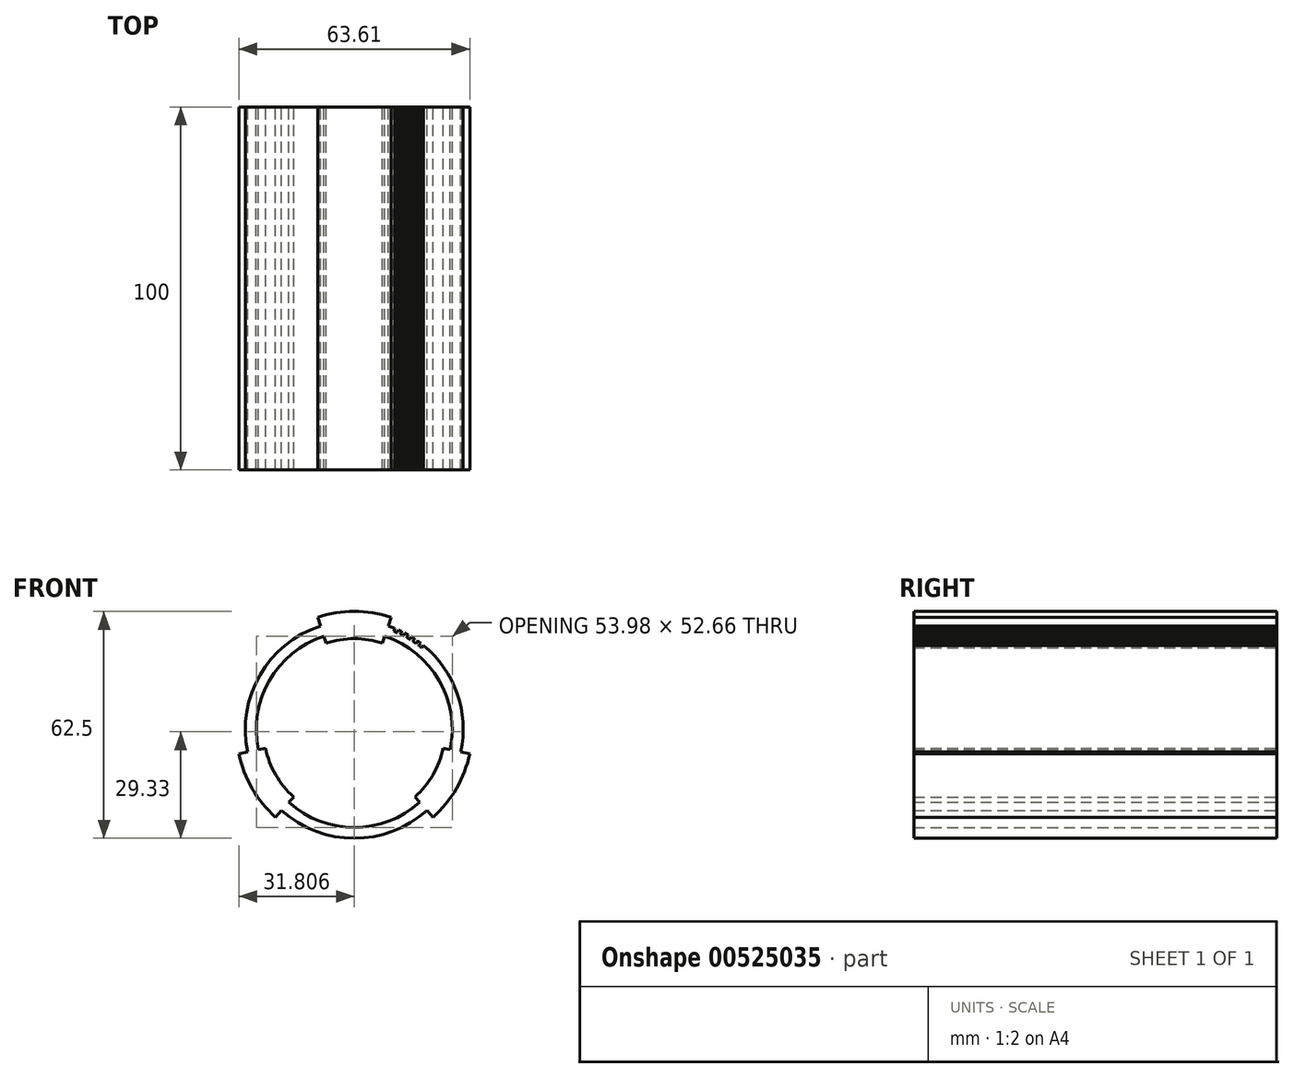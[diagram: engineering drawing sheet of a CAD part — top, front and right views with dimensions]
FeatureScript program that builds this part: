
annotation { "Feature Type Name" : "Feature", "Feature Type Description" : "" }
export const myFeature = defineFeature(function(context is Context, id is Id, definition is map)
    precondition{}
    {
        {
            var Q0;
            Q0=qCreatedBy(makeId("Front.planeOp"),FACE);
            var sketch = newSketch(context, id + "F0", { "sketchPlane" : qUnion([Q0])});
            skArc(sketch, "E0", {"start": v(-14.55, 20.43) * mm, "mid": v(-31.2, 6.92) * mm, "end": v(-34.58, -14.27) * mm});
            skArc(sketch, "E1.0", {"start": v(-13.61, 17.58) * mm, "mid": v(-28.6, 5.42) * mm, "end": v(-31.64, -13.65) * mm});
            skLineSegment(sketch, "E2", {"start": v(-13, 15.68) * mm, "end": v(-13.61, 17.58) * mm});
            skLineSegment(sketch, "E3.MirrorCS", {"start": v(2.54, 15.68) * mm, "end": v(3.17, 17.58) * mm});
            skArc(sketch, "E4.trimOffspring", {"start": v(4.87, 22.8) * mm, "mid": v(-5.22, 24.42) * mm, "end": v(-15.32, 22.8) * mm});
            skArc(sketch, "E5.trimOffspring", {"start": v(2.54, 15.68) * mm, "mid": v(-5.22, 16.92) * mm, "end": v(-13, 15.68) * mm});
            skPoint(sketch, "E6.start.orphan", {"position": v(-15.32, -38.97) * mm});
            skPoint(sketch, "E7.trimOffspring.end.orphan", {"position": v(4.87, -38.97) * mm});
            skLineSegment(sketch, "E8.trimOffspring", {"start": v(-14.55, 20.43) * mm, "end": v(-15.32, 22.8) * mm});
            skLineSegment(sketch, "E9.trimOffspring", {"start": v(4.1, 20.43) * mm, "end": v(4.87, 22.8) * mm});
            skLineSegment(sketch, "E10", {"start": v(-5.22, -8.08) * mm, "end": v(-5.22, 24.42) * mm});
            skArc(sketch, "E11.1.0", {"start": v(-37.03, -14.78) * mm, "mid": v(-33.37, -24.33) * mm, "end": v(-26.93, -32.27) * mm});
            skArc(sketch, "E11.1.1", {"start": v(-29.69, -13.23) * mm, "mid": v(-26.88, -20.58) * mm, "end": v(-21.92, -26.7) * mm});
            skLineSegment(sketch, "E11.1.2", {"start": v(-25.26, -30.41) * mm, "end": v(-26.93, -32.27) * mm});
            skLineSegment(sketch, "E11.1.3", {"start": v(-21.92, -26.7) * mm, "end": v(-23.25, -28.18) * mm});
            skLineSegment(sketch, "E11.1.4", {"start": v(-29.69, -13.23) * mm, "end": v(-31.64, -13.65) * mm});
            skLineSegment(sketch, "E11.1.5", {"start": v(-34.58, -14.27) * mm, "end": v(-37.03, -14.78) * mm});
            skArc(sketch, "E11.2.0", {"start": v(16.48, -32.27) * mm, "mid": v(22.92, -24.33) * mm, "end": v(26.58, -14.78) * mm});
            skArc(sketch, "E11.2.1", {"start": v(11.47, -26.7) * mm, "mid": v(16.43, -20.58) * mm, "end": v(19.24, -13.23) * mm});
            skLineSegment(sketch, "E11.2.2", {"start": v(24.13, -14.27) * mm, "end": v(26.58, -14.78) * mm});
            skLineSegment(sketch, "E11.2.3", {"start": v(19.24, -13.23) * mm, "end": v(21.2, -13.65) * mm});
            skLineSegment(sketch, "E11.2.4", {"start": v(11.47, -26.7) * mm, "end": v(12.8, -28.18) * mm});
            skLineSegment(sketch, "E11.2.5", {"start": v(14.8, -30.41) * mm, "end": v(16.48, -32.27) * mm});
            skArc(sketch, "E12.trimOffspring", {"start": v(21.2, -13.65) * mm, "mid": v(18.16, 5.42) * mm, "end": v(3.17, 17.58) * mm});
            skArc(sketch, "E13.trimOffspring", {"start": v(24.13, -14.27) * mm, "mid": v(23.1, 1.83) * mm, "end": v(13.87, 15.06) * mm});
            skArc(sketch, "E14.trimOffspring", {"start": v(-23.25, -28.18) * mm, "mid": v(-5.22, -35.08) * mm, "end": v(12.8, -28.18) * mm});
            skArc(sketch, "E15.trimOffspring", {"start": v(-25.26, -30.41) * mm, "mid": v(-5.22, -38.08) * mm, "end": v(14.8, -30.41) * mm});
            skLineSegment(sketch, "E16", {"start": v(5.68, 18.96) * mm, "end": v(6, 19.74) * mm});
            skLineSegment(sketch, "E17.1.0", {"start": v(6.6, 18.57) * mm, "end": v(6.94, 19.34) * mm});
            skLineSegment(sketch, "E17.2.0", {"start": v(7.5, 18.15) * mm, "end": v(7.86, 18.91) * mm});
            skLineSegment(sketch, "E17.3.0", {"start": v(8.38, 17.7) * mm, "end": v(8.77, 18.45) * mm});
            skLineSegment(sketch, "E17.4.0", {"start": v(9.25, 17.22) * mm, "end": v(9.67, 17.96) * mm});
            skLineSegment(sketch, "E17.5.0", {"start": v(10.1, 16.72) * mm, "end": v(10.55, 17.44) * mm});
            skLineSegment(sketch, "E17.6.0", {"start": v(10.94, 16.18) * mm, "end": v(11.4, 16.89) * mm});
            skLineSegment(sketch, "E17.7.0", {"start": v(11.75, 15.62) * mm, "end": v(12.25, 16.3) * mm});
            skLineSegment(sketch, "E17.8.0", {"start": v(12.55, 15.02) * mm, "end": v(13.07, 15.7) * mm});
            skLineSegment(sketch, "E17.9.0", {"start": v(13.33, 14.4) * mm, "end": v(13.87, 15.06) * mm});
            skLineSegment(sketch, "E17.anchor1", {"start": v(5.68, 18.96) * mm, "end": v(6, 19.74) * mm, "construction": true});
            skLineSegment(sketch, "E17.anchor2", {"start": v(13.33, 14.4) * mm, "end": v(13.87, 15.06) * mm, "construction": true});
            skArc(sketch, "E18", {"start": v(13.33, 14.4) * mm, "mid": v(12.94, 14.72) * mm, "end": v(12.55, 15.02) * mm});
            skArc(sketch, "E19.trimOffspring", {"start": v(6.6, 18.57) * mm, "mid": v(6.14, 18.77) * mm, "end": v(5.68, 18.96) * mm});
            skArc(sketch, "E20.trimOffspring", {"start": v(8.38, 17.7) * mm, "mid": v(7.94, 17.93) * mm, "end": v(7.5, 18.15) * mm});
            skArc(sketch, "E21.trimOffspring", {"start": v(10.1, 16.72) * mm, "mid": v(9.68, 16.97) * mm, "end": v(9.25, 17.22) * mm});
            skArc(sketch, "E22.trimOffspring", {"start": v(11.75, 15.62) * mm, "mid": v(11.35, 15.9) * mm, "end": v(10.94, 16.18) * mm});
            skArc(sketch, "E23.trimOffspring", {"start": v(6, 19.74) * mm, "mid": v(5.05, 20.1) * mm, "end": v(4.1, 20.43) * mm});
            skArc(sketch, "E24.trimOffspring", {"start": v(7.86, 18.91) * mm, "mid": v(7.4, 19.13) * mm, "end": v(6.94, 19.34) * mm});
            skArc(sketch, "E25.trimOffspring", {"start": v(9.67, 17.96) * mm, "mid": v(9.22, 18.21) * mm, "end": v(8.77, 18.45) * mm});
            skArc(sketch, "E26.trimOffspring", {"start": v(11.4, 16.89) * mm, "mid": v(10.98, 17.17) * mm, "end": v(10.55, 17.44) * mm});
            skArc(sketch, "E27.trimOffspring", {"start": v(13.07, 15.7) * mm, "mid": v(12.66, 16) * mm, "end": v(12.25, 16.3) * mm});
            skSolve(sketch);
        }
        {
            var Q0;
            Q0=makeQuery(id+"F0.imprint","IMPRINT",FACE,{"disambiguationData":[TD([[makeQuery(id+"F0.imprint","IMPRINT",EDGE,{"derivedFrom":sQuery(id+"F0.wireOp",EDGE,"E0")}),1.0]])]});
            extrude(context, id + "F1", {"entities" : qUnion([Q0]), "depth" : 100 * mm, "offsetDistance" : 25 * mm});
        }
    });
